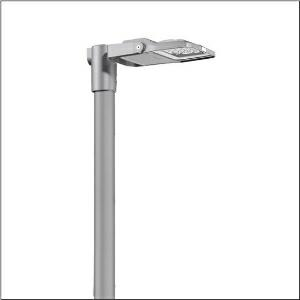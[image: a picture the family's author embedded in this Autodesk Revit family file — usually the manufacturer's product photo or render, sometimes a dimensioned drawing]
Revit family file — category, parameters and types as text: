
# Revit family: floodlight_fl_21_iq_micro___pl64_5xa7762a2e3a_859a
name_source: partatom
category: Lighting Fixtures
units: mm (PartAtom-declared; Revit-internal decimal feet)

## family parameters
Cut with Voids When Loaded = No
Host = Face
Light Source = No
Part Type = Normal
Room Calculation Point = No
Round Connector Dimension = Use Diameter
Shared = No

## types (1)
- --- (1 x LED, 2870 lm, 23.1 W, 3000K)
    Apparent Load = 23 VA
    CIE Flux Codes = 28 80 98 100 100
    Color Rendering = 70
    Color Temperature = 3000K
    Default Elevation = 1800 mm
    Description = Floodlight FL 21 iQ micro, floodlight, primary light control with lens, of PMMA, primary optical cover: protective disc, of toughened safety glass, transparent, light distribution: PL64, light emission: direct distribution, installation type: surface-mounted, LED, High Power LED, rated luminous flux: 2.870lm, luminous efficacy: 124lm/W, light colour: 730, colour temperature: 3000K, control gear: iQ Street-Remote/DALI, control: Auto-Match, Temp-Guard, Night-Set, Smart-Wire, Desk-Remote (wireless, voltage-free reading and setting of iQ features in the workshop via application-optimized NFC function/RFID function), optimised constant luminous flux control (CLO 2.0), Street-Remote, with terminal, 6-pole, mains connection: 220..240V, AC, 50/60Hz, start of lifetime: 23W, end of service life: 24W, reduction: 11W, luminaire housing, of diecast aluminium, powder-coated, Siteco® metallic grey (DB 702S), corrosivity category C5 mid according to DIN EN ISO 12944, suitable for swimming pools, chlorine-resistant, sealing non-destructively replaceable, please order mast flange separately, mast bracket, of steel, galvanised, powder-coated, Siteco® metallic grey (DB 702S), protection rating (complete): IP66, insulation class (complete): insulation class II (safety insulation), certification: CE, ENEC, VDE, protection symbol: D, impact resistance: IK07, permissible operating ambient temperature: -40..+40°C, permissible operating ambient temperature for outdoor applications: -40..+50°C, standard: DIN EN 12944, LABS conformity tested according to VDMA 24364:2018-05, packaging unit: 1 piece

Light Distribution: PL64
    Height = 65 mm
    Lamp = 1 x LED
    Lamp Light Flux = 2870 lm
    Lamp Power = 23.1 W
    Lamp count = 1
    Length = 312 mm
    Luminous efficacy = 124 lm/W
    Manufacturer = Siteco
    ModVariant = No
    Model = 5XA7762A2E3A
    Number of Poles = 1
    OnlyDefault = Yes
    Power Factor = 1
    Product Name = Floodlight FL 21 iQ micro | PL64
    Product group = floodlight | pylon annexe
    ProductGroupID = 6200
    Protection Class = Protection class II
    Protection Degree = IP 66
    RLX_Detail_Level = 1
    RLX_Emergency_Light_Flux = 0 lm
    RLX_Emergency_Type = 0
    RLX_Emergency_Type_DB = No
    RlxData = <blob elided: 101777 chars, md5=32f77cb6>
    Socket = socket
    Standby Power = 0 W
    System Light Flux = 2870 lm
    System Power = 23 W
    Type Comments = factory setting: luminous flux: 100 % | dim-lin: 254 | 455 mA
    Type Image = l_1007121.jpg
    URL = http://relux.com
    VarID = @adj_180578
    Voltage = 0 V
    Weight = 0.00 kg
    Width = 230 mm

## geometry (parser evidence)
native form markers: Blend x4, Sweep x11
no freeform markers — native parametric forms only
